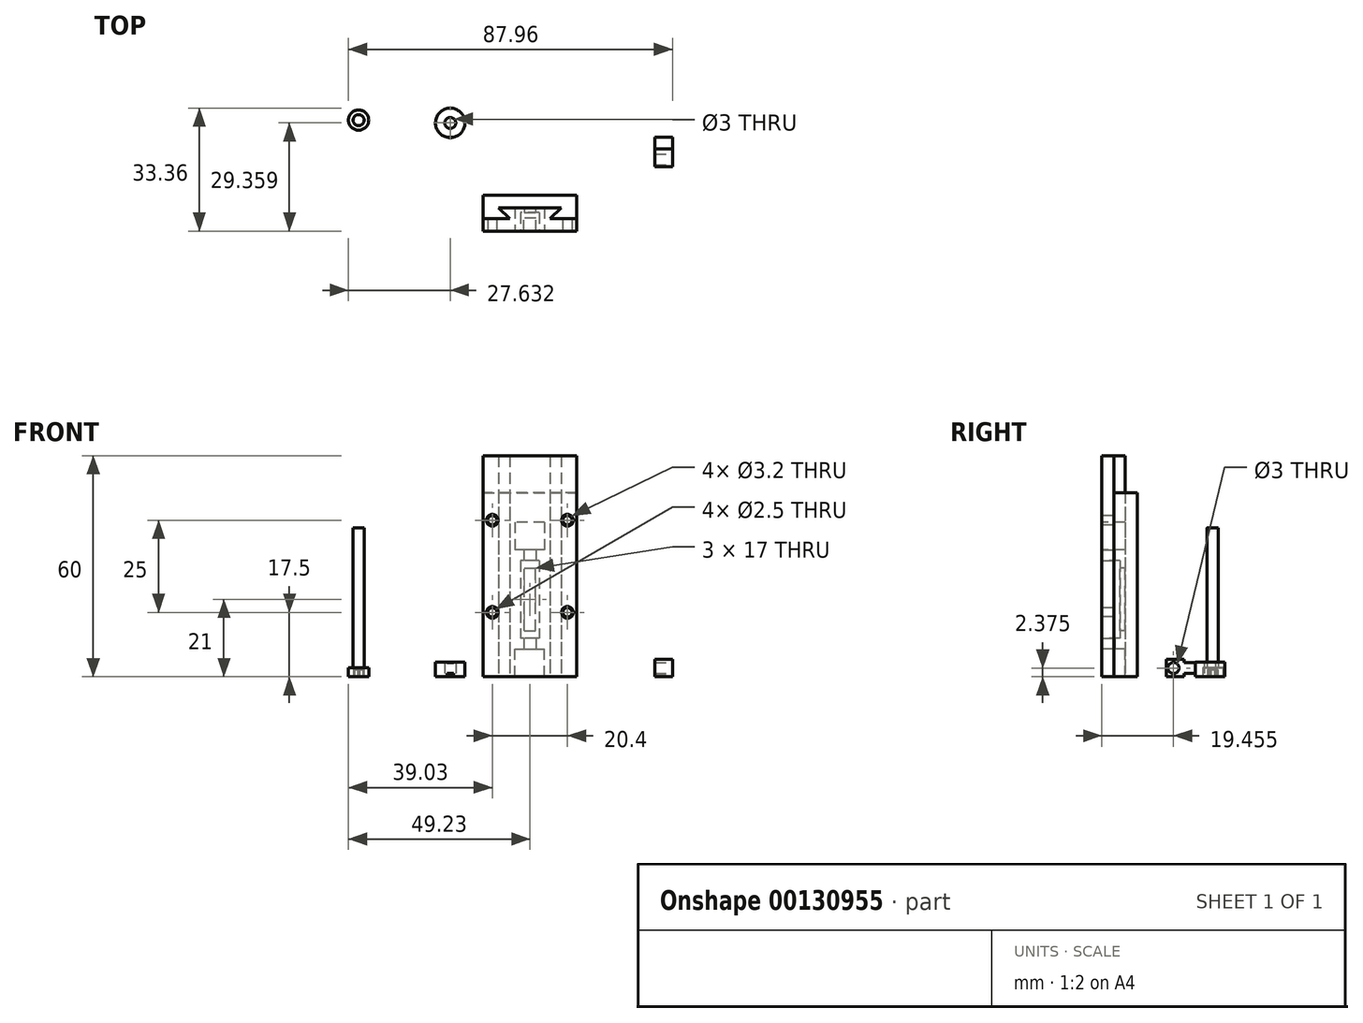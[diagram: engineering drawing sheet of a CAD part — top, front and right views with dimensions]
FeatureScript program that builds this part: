
annotation { "Feature Type Name" : "Feature", "Feature Type Description" : "" }
export const myFeature = defineFeature(function(context is Context, id is Id, definition is map)
    precondition{}
    {
        {
            var Q0;
            Q0=qCreatedBy(makeId("Top.planeOp"),FACE);
            var sketch = newSketch(context, id + "F0", { "sketchPlane" : qUnion([Q0])});
            skLineSegment(sketch, "E0", {"start": v(-12.7, 0) * mm, "end": v(12.7, 0) * mm});
            skLineSegment(sketch, "E1", {"start": v(12.7, 0) * mm, "end": v(12.7, 3.35) * mm});
            skLineSegment(sketch, "E2", {"start": v(12.7, 3.35) * mm, "end": v(5.5, 3.35) * mm});
            skLineSegment(sketch, "E3", {"start": v(5.5, 3.35) * mm, "end": v(8.5, 6.35) * mm});
            skLineSegment(sketch, "E4", {"start": v(8.5, 6.35) * mm, "end": v(-8.5, 6.35) * mm});
            skLineSegment(sketch, "E5", {"start": v(-8.5, 6.35) * mm, "end": v(-5.5, 3.35) * mm});
            skLineSegment(sketch, "E6", {"start": v(-5.5, 3.35) * mm, "end": v(-12.7, 3.35) * mm});
            skLineSegment(sketch, "E7", {"start": v(-12.7, 3.35) * mm, "end": v(-12.7, 0) * mm});
            skSolve(sketch);
        }
        {
            var Q0;
            Q0 = qSketchRegion(id + "F0", true);
            extrude(context, id + "F1", {"entities" : qUnion([Q0]), "depth" : 60 * mm});
        }
        {
            var Q0;
            Q0=makeQuery(id+"F1.opExtrude","SWEPT_FACE",FACE,{"disambiguationData":[OSD([sQuery(id+"F0.wireOp",EDGE,"E0")])]});
            var sketch = newSketch(context, id + "F2", { "sketchPlane" : qUnion([Q0])});
            skLineSegment(sketch, "E8.left", {"start": v(-1.6, 42) * mm, "end": v(-1.6, 0) * mm});
            skLineSegment(sketch, "E8.right", {"start": v(1.6, 42) * mm, "end": v(1.6, 0) * mm});
            skLineSegment(sketch, "E9", {"start": v(-1.6, 42) * mm, "end": v(1.6, 42) * mm});
            skLineSegment(sketch, "E10", {"start": v(1.6, 0) * mm, "end": v(-1.6, 0) * mm});
            skSolve(sketch);
        }
        {
            var Q0;
            Q0 = qSketchRegion(id + "F2", true);
            extrude(context, id + "F3", {"entities" : qUnion([Q0]), "operationType" : NewBodyOperationType.REMOVE, "oppositeDirection" : true, "depth" : 3.5 * mm});
        }
        {
            var Q0;
            Q0=makeQuery(id+"F1.opExtrude","SWEPT_FACE",FACE,{"disambiguationData":[OSD([sQuery(id+"F0.wireOp",EDGE,"E0")])]});
            var sketch = newSketch(context, id + "F4", { "sketchPlane" : qUnion([Q0])});
            skLineSegment(sketch, "E11.bottom", {"start": v(4, 42) * mm, "end": v(-4, 42) * mm});
            skLineSegment(sketch, "E11.top", {"start": v(4, 34.5) * mm, "end": v(-4, 34.5) * mm});
            skLineSegment(sketch, "E11.left", {"start": v(4, 42) * mm, "end": v(4, 34.5) * mm});
            skLineSegment(sketch, "E11.right", {"start": v(-4, 42) * mm, "end": v(-4, 34.5) * mm});
            skLineSegment(sketch, "E12.bottom", {"start": v(-4, 0) * mm, "end": v(4, 0) * mm});
            skLineSegment(sketch, "E12.top", {"start": v(-4, 7.5) * mm, "end": v(4, 7.5) * mm});
            skLineSegment(sketch, "E12.left", {"start": v(-4, 0) * mm, "end": v(-4, 7.5) * mm});
            skLineSegment(sketch, "E12.right", {"start": v(4, 0) * mm, "end": v(4, 7.5) * mm});
            skSolve(sketch);
        }
        {
            var Q0;
            Q0 = qSketchRegion(id + "F4", true);
            extrude(context, id + "F5", {"entities" : qUnion([Q0]), "operationType" : NewBodyOperationType.REMOVE, "endBound" : BoundingType.THROUGH_ALL, "oppositeDirection" : true, "depth" : 6 * mm});
        }
        {
            var Q0;
            Q0=makeQuery(id+"F1.opExtrude","SWEPT_FACE",FACE,{"disambiguationData":[OSD([sQuery(id+"F0.wireOp",EDGE,"E0")])]});
            var sketch = newSketch(context, id + "F6", { "sketchPlane" : qUnion([Q0])});
            skLineSegment(sketch, "E13.bottom", {"start": v(2.5, 31.5) * mm, "end": v(-2.5, 31.5) * mm});
            skLineSegment(sketch, "E13.top", {"start": v(2.5, 10.5) * mm, "end": v(-2.5, 10.5) * mm});
            skLineSegment(sketch, "E13.left", {"start": v(2.5, 31.5) * mm, "end": v(2.5, 10.5) * mm});
            skLineSegment(sketch, "E13.right", {"start": v(-2.5, 31.5) * mm, "end": v(-2.5, 10.5) * mm});
            skPoint(sketch, "E14", {"position": v(0, 10.5) * mm});
            skSolve(sketch);
        }
        {
            var Q0;
            Q0 = qSketchRegion(id + "F6", true);
            extrude(context, id + "F7", {"entities" : qUnion([Q0]), "operationType" : NewBodyOperationType.REMOVE, "oppositeDirection" : true, "depth" : 5 * mm});
        }
        {
            var Q0;
            Q0=qCreatedBy(makeId("Top.planeOp"),FACE);
            var sketch = newSketch(context, id + "F8", { "sketchPlane" : qUnion([Q0])});
            skCircle(sketch, "E15", {"center": v(-46.48, 30.12) * mm, "radius": 2.75 * mm});
            skSolve(sketch);
        }
        {
            var Q0;
            Q0 = qSketchRegion(id + "F8", true);
            extrude(context, id + "F9", {"entities" : qUnion([Q0]), "depth" : 2.5 * mm});
        }
        {
            var Q0;
            Q0=makeQuery(id+"F9.opExtrude","CAP_FACE",FACE,{"disambiguationData":[OSD([sQuery(id+"F8.wireOp",EDGE,"E15")])],"isStart":false});
            var sketch = newSketch(context, id + "F10", { "sketchPlane" : qUnion([Q0])});
            skCircle(sketch, "E16", {"center": v(-46.48, 30.12) * mm, "radius": 1.5 * mm});
            skSolve(sketch);
        }
        {
            var Q0;
            Q0 = qSketchRegion(id + "F10", true);
            extrude(context, id + "F11", {"entities" : qUnion([Q0]), "operationType" : NewBodyOperationType.ADD, "depth" : 38 * mm});
        }
        {
            var Q0;
            Q0=makeQuery(id+"F9.opExtrude","CAP_FACE",FACE,{"disambiguationData":[OSD([sQuery(id+"F8.wireOp",EDGE,"E15")])],"isStart":true});
            var sketch = newSketch(context, id + "F12", { "sketchPlane" : qUnion([Q0])});
            skCircle(sketch, "E17.cCircle", {"center": v(-46.48, -30.12) * mm, "radius": 1.25 * mm, "construction": true});
            skLineSegment(sketch, "E17.0", {"start": v(-47.83, -29.62) * mm, "end": v(-46.72, -28.7) * mm});
            skLineSegment(sketch, "E17.1", {"start": v(-46.72, -28.7) * mm, "end": v(-45.37, -29.2) * mm});
            skLineSegment(sketch, "E17.2", {"start": v(-45.37, -29.2) * mm, "end": v(-45.12, -30.62) * mm});
            skLineSegment(sketch, "E17.3", {"start": v(-45.12, -30.62) * mm, "end": v(-46.23, -31.55) * mm});
            skLineSegment(sketch, "E17.4", {"start": v(-46.23, -31.55) * mm, "end": v(-47.59, -31.05) * mm});
            skLineSegment(sketch, "E17.5", {"start": v(-47.59, -31.05) * mm, "end": v(-47.83, -29.62) * mm});
            skPoint(sketch, "E17.0.midPoint", {"position": v(-47.28, -29.16) * mm});
            skSolve(sketch);
        }
        {
            var Q0;
            Q0=qCreatedBy(makeId("Top.planeOp"),FACE);
            var sketch = newSketch(context, id + "F13", { "sketchPlane" : qUnion([Q0])});
            skCircle(sketch, "E18", {"center": v(-21.6, 29.36) * mm, "radius": 1.5 * mm});
            skCircle(sketch, "E19", {"center": v(-21.6, 29.36) * mm, "radius": 4 * mm});
            skSolve(sketch);
        }
        {
            var Q0;
            Q0 = qSketchRegion(id + "F13", true);
            extrude(context, id + "F14", {"entities" : qUnion([Q0]), "depth" : 4 * mm});
        }
        {
            var Q0;
            Q0 = qSketchRegion(id + "F12", true);
            extrude(context, id + "F15", {"entities" : qUnion([Q0]), "operationType" : NewBodyOperationType.REMOVE, "oppositeDirection" : true, "depth" : 2 * mm});
        }
        {
            var Q0;
            Q0=makeQuery(id+"F7.boolean.opBoolean","COPY",FACE,{"derivedFrom":makeQuery(id+"F7.opExtrude","CAP_FACE",FACE,{"disambiguationData":[OSD([sQuery(id+"F6.wireOp",EDGE,"E13.bottom"),sQuery(id+"F6.wireOp",EDGE,"E13.top"),sQuery(id+"F6.wireOp",EDGE,"E13.left"),sQuery(id+"F6.wireOp",EDGE,"E13.right")])],"isStart":false})});
            var sketch = newSketch(context, id + "F16", { "sketchPlane" : qUnion([Q0])});
            skLineSegment(sketch, "E20.bottom", {"start": v(-1.5, 12.5) * mm, "end": v(1.5, 12.5) * mm});
            skLineSegment(sketch, "E20.top", {"start": v(-1.5, 29.5) * mm, "end": v(1.5, 29.5) * mm});
            skLineSegment(sketch, "E20.left", {"start": v(-1.5, 12.5) * mm, "end": v(-1.5, 29.5) * mm});
            skLineSegment(sketch, "E20.right", {"start": v(1.5, 12.5) * mm, "end": v(1.5, 29.5) * mm});
            skPoint(sketch, "E20.middle", {"position": v(0, 21) * mm});
            skLineSegment(sketch, "E21", {"start": v(-2.5, 21) * mm, "end": v(0, 21) * mm, "construction": true});
            skSolve(sketch);
        }
        {
            var Q0;
            Q0 = qSketchRegion(id + "F16", true);
            extrude(context, id + "F17", {"entities" : qUnion([Q0]), "operationType" : NewBodyOperationType.REMOVE, "endBound" : BoundingType.THROUGH_ALL, "oppositeDirection" : true, "depth" : 25 * mm});
        }
        {
            var Q0;
            Q0=makeQuery(id+"F1.opExtrude","SWEPT_FACE",FACE,{"disambiguationData":[OSD([sQuery(id+"F0.wireOp",EDGE,"E0")])]});
            var sketch = newSketch(context, id + "F18", { "sketchPlane" : qUnion([Q0])});
            skCircle(sketch, "E22", {"center": v(10.2, 17.5) * mm, "radius": 1.25 * mm});
            skCircle(sketch, "E23", {"center": v(-10.2, 17.5) * mm, "radius": 1.25 * mm});
            skLineSegment(sketch, "E24", {"start": v(12.7, 30) * mm, "end": v(-12.7, 30) * mm, "construction": true});
            skCircle(sketch, "E25.MirrorC", {"center": v(10.2, 42.5) * mm, "radius": 1.25 * mm});
            skCircle(sketch, "E26.MirrorC", {"center": v(-10.2, 42.5) * mm, "radius": 1.25 * mm});
            skSolve(sketch);
        }
        {
            var Q0;
            Q0 = qSketchRegion(id + "F18", true);
            extrude(context, id + "F19", {"entities" : qUnion([Q0]), "operationType" : NewBodyOperationType.REMOVE, "endBound" : BoundingType.UP_TO_NEXT, "oppositeDirection" : true, "depth" : 25 * mm});
        }
        {
            var Q0;
            Q0=makeQuery(id+"F1.opExtrude","SWEPT_FACE",FACE,{"disambiguationData":[OSD([sQuery(id+"F0.wireOp",EDGE,"E0")])]});
            var sketch = newSketch(context, id + "F20", { "sketchPlane" : qUnion([Q0])});
            skLineSegment(sketch, "E27.bottom", {"start": v(12.7, 0) * mm, "end": v(-12.7, 0) * mm});
            skLineSegment(sketch, "E27.left", {"start": v(12.7, 0) * mm, "end": v(12.7, 60) * mm});
            skLineSegment(sketch, "E27.right", {"start": v(-12.7, 0) * mm, "end": v(-12.7, 60) * mm});
            skCircle(sketch, "E28", {"center": v(10.2, 42.5) * mm, "radius": 1.6 * mm});
            skCircle(sketch, "E29", {"center": v(-10.2, 42.5) * mm, "radius": 1.6 * mm});
            skCircle(sketch, "E30", {"center": v(-10.2, 17.5) * mm, "radius": 1.6 * mm});
            skCircle(sketch, "E31", {"center": v(10.2, 17.5) * mm, "radius": 1.6 * mm});
            skLineSegment(sketch, "E32", {"start": v(-12.7, 60) * mm, "end": v(12.7, 60) * mm});
            skSolve(sketch);
        }
        {
            var Q0;
            Q0 = qSketchRegion(id + "F20", true);
            extrude(context, id + "F21", {"entities" : qUnion([Q0]), "depth" : 1 / 203.2 * mm});
        }
        {
            var Q0;
            Q0=qCreatedBy(makeId("Top.planeOp"),FACE);
            var sketch = newSketch(context, id + "F22", { "sketchPlane" : qUnion([Q0])});
            skLineSegment(sketch, "E33", {"start": v(-12.7, 9.7) * mm, "end": v(12.7, 9.7) * mm});
            skLineSegment(sketch, "E34", {"start": v(12.7, 9.7) * mm, "end": v(12.7, 3.35) * mm});
            skLineSegment(sketch, "E35", {"start": v(12.7, 3.35) * mm, "end": v(5.5, 3.35) * mm});
            skLineSegment(sketch, "E36", {"start": v(5.5, 3.35) * mm, "end": v(8.5, 6.35) * mm});
            skLineSegment(sketch, "E37", {"start": v(8.5, 6.35) * mm, "end": v(-8.5, 6.35) * mm});
            skLineSegment(sketch, "E38", {"start": v(-8.5, 6.35) * mm, "end": v(-5.5, 3.35) * mm});
            skLineSegment(sketch, "E39", {"start": v(-5.5, 3.35) * mm, "end": v(-12.7, 3.35) * mm});
            skLineSegment(sketch, "E40", {"start": v(-12.7, 3.35) * mm, "end": v(-12.7, 9.7) * mm});
            skSolve(sketch);
        }
        {
            var Q0;
            Q0 = qSketchRegion(id + "F22", true);
            extrude(context, id + "F23", {"entities" : qUnion([Q0]), "depth" : 50 * mm});
        }
        {
            var Q0;
            Q0=qCreatedBy(makeId("Top.planeOp"),FACE);
            var sketch = newSketch(context, id + "F24", { "sketchPlane" : qUnion([Q0])});
            skLineSegment(sketch, "E41.bottom", {"start": v(33.98, 25.45) * mm, "end": v(38.73, 25.45) * mm});
            skLineSegment(sketch, "E41.top", {"start": v(33.98, 17.45) * mm, "end": v(38.73, 17.45) * mm});
            skLineSegment(sketch, "E41.left", {"start": v(33.98, 25.45) * mm, "end": v(33.98, 17.45) * mm});
            skLineSegment(sketch, "E41.right", {"start": v(38.73, 25.45) * mm, "end": v(38.73, 17.45) * mm});
            skSolve(sketch);
        }
        {
            var Q0;
            Q0 = qSketchRegion(id + "F24", true);
            extrude(context, id + "F25", {"entities" : qUnion([Q0]), "depth" : 4.75 * mm});
        }
        {
            var Q0;
            Q0=makeQuery(id+"F25.opExtrude","SWEPT_FACE",FACE,{"disambiguationData":[OSD([sQuery(id+"F24.wireOp",EDGE,"E41.right")])]});
            var sketch = newSketch(context, id + "F26", { "sketchPlane" : qUnion([Q0])});
            skCircle(sketch, "E42", {"center": v(19.45, 2.38) * mm, "radius": 1.5 * mm});
            skSolve(sketch);
        }
        {
            var Q0;
            Q0 = qSketchRegion(id + "F26", true);
            extrude(context, id + "F27", {"entities" : qUnion([Q0]), "operationType" : NewBodyOperationType.REMOVE, "endBound" : BoundingType.THROUGH_ALL, "oppositeDirection" : true, "depth" : 25 * mm});
        }
        {
            var Q0;
            Q0=makeQuery(id+"F25.opExtrude","SWEPT_FACE",FACE,{"disambiguationData":[OSD([sQuery(id+"F24.wireOp",EDGE,"E41.right")])]});
            var sketch = newSketch(context, id + "F28", { "sketchPlane" : qUnion([Q0])});
            skLineSegment(sketch, "E43.bottom", {"start": v(25.45, 4.75) * mm, "end": v(22.35, 4.75) * mm});
            skLineSegment(sketch, "E43.top", {"start": v(25.45, 3.82) * mm, "end": v(22.35, 3.82) * mm});
            skLineSegment(sketch, "E43.left", {"start": v(25.45, 4.75) * mm, "end": v(25.45, 3.82) * mm});
            skLineSegment(sketch, "E43.right", {"start": v(22.35, 4.75) * mm, "end": v(22.35, 3.82) * mm});
            skLineSegment(sketch, "E44.bottom", {"start": v(25.45, 0) * mm, "end": v(22.35, 0) * mm});
            skLineSegment(sketch, "E44.top", {"start": v(25.45, 0.92) * mm, "end": v(22.35, 0.92) * mm});
            skLineSegment(sketch, "E44.left", {"start": v(25.45, 0) * mm, "end": v(25.45, 0.93) * mm});
            skLineSegment(sketch, "E44.right", {"start": v(22.35, 0) * mm, "end": v(22.35, 0.92) * mm});
            skSolve(sketch);
        }
        {
            var Q0;
            Q0 = qSketchRegion(id + "F28", true);
            extrude(context, id + "F29", {"entities" : qUnion([Q0]), "operationType" : NewBodyOperationType.REMOVE, "endBound" : BoundingType.THROUGH_ALL, "oppositeDirection" : true, "depth" : 25 * mm});
        }
    });
